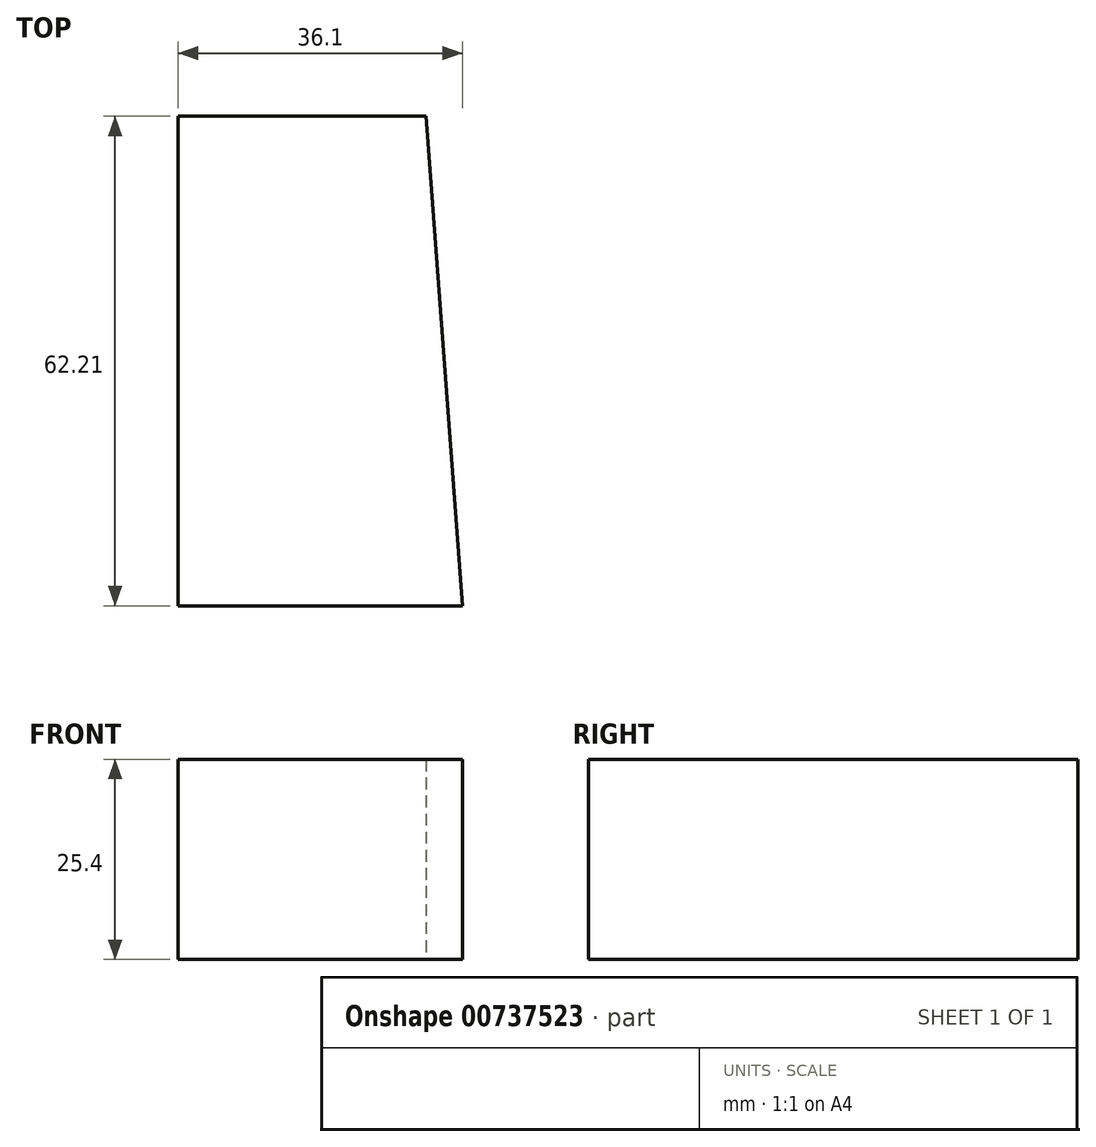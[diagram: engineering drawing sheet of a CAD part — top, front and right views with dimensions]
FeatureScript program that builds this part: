
annotation { "Feature Type Name" : "Feature", "Feature Type Description" : "" }
export const myFeature = defineFeature(function(context is Context, id is Id, definition is map)
    precondition{}
    {
        {
            var Q0;
            Q0=qCreatedBy(makeId("Top.planeOp"),FACE);
            var sketch = newSketch(context, id + "F0", { "sketchPlane" : qUnion([Q0])});
            skLineSegment(sketch, "E0", {"start": v(-125.83, 0) * mm, "end": v(-125.83, -62.2) * mm});
            skLineSegment(sketch, "E1", {"start": v(-125.83, -62.2) * mm, "end": v(-89.73, -62.2) * mm});
            skLineSegment(sketch, "E2", {"start": v(-89.73, -62.2) * mm, "end": v(-94.37, 0) * mm});
            skLineSegment(sketch, "E3", {"start": v(-94.37, 0) * mm, "end": v(-125.83, 0) * mm});
            skSolve(sketch);
        }
        {
            var Q0;
            Q0 = qSketchRegion(id + "F0", true);
            extrude(context, id + "F1", {"entities" : qUnion([Q0]), "depth" : 25.4 * mm, "offsetDistance" : 25.4 * mm});
        }
    });
